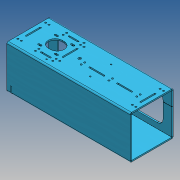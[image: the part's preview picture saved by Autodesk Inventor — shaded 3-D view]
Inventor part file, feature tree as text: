
AUTODESK INVENTOR PART (.ipt)
format: ipt  version: 2017 (Build 210142000, 142)  size: 519,168 bytes
history: native  units: mm
features: other x15, sketch x5, extrude x3, projected_geometry x1
ambient origin geometry x8: Origin, YZ Plane, XZ Plane, XY Plane, X Axis, Y Axis, Z Axis, Center Point
bodies: Body1 (feature_tree)
feature tree (24):
  other  "Sólido1"
  extrude  "Extrusión1"  Depth=67.5mm
  other  "Pestaña1"
  sketch  "Boceto4"  dims[d9=41.14mm]
  other  "Cara1"
  other  "Cara2"
  sketch  "Boceto5"  dims[d10=6.0mm d11=53.14mm d12=6.0mm d13=4.0mm d14=115.0mm d15=20.0mm d16=60.0mm d17=60.0mm d18=4.0mm d19=33.93mm d20=22.0mm d21=120.0mm d22=130.0mm d23=20.0mm d24=4.0mm d25=0.0mm d26=4.0mm d27=2.0mm d28=8.0mm d29=4.0mm d30=120.0mm d31=90.0deg d32=0.1mm d33=16.0mm d34=4.0mm d35=4.0mm d36=4.0mm d37=8.0mm d38=25.0mm d39=25.0mm d40=4.0mm d41=0.0mm d42=47.14mm d43=47.14mm d44=20.0mm d45=6.0mm d46=14.2mm d47=25.0mm d48=0.1mm d49=4.0mm d50=2.0mm d51=8.0mm d52=4.0mm d53=0.1mm d54=4.0mm d55=2.0mm d56=8.0mm d57=4.0mm d58=0.5mm d59=0.5mm d60=20.0mm d61=20.0mm d62=4.0mm d63=41.0mm d65=5.0mm d66=10.0mm d67=5.0mm d68=40.0mm d70=4.0mm d71=25.0mm d72=25.0mm d73=0.1mm d74=4.0mm d75=2.0mm d76=8.0mm d77=4.0mm d78=4.0mm d79=41.0mm d80=39.833333mm d81=79.666667mm d82=84.0mm d83=5.0mm d84=20.0mm d85=0.0mm d86=50.0mm d87=355.0mm d88=12.5mm d89=12.5mm d90=23.6mm d91=11.8mm d92=26.0mm d93=15.0mm d94=80.0mm d95=40.0mm d96=4.0mm d97=194.8mm d98=97.4mm]
  other  "Cara3"
  extrude  "Extrusión3"  Depth=42.0mm
  extrude  "Extrusión2"  Depth=5.0mm
  sketch  "Boceto1"  dims[d1=56.4mm d2=67.5mm]
  sketch  "Boceto2"  dims[d4=200.0mm d5=42.0mm]
  other  "Placa1"
  other  "Doblez1"
  other  "Esquina1"
  sketch  "Boceto3"  dims[d6=8.0mm d8=5.0mm]
  projected_geometry  "Contorno proyectado1"
  other  "Placa2"
  other  "Doblez2"
  other  "Placa3"
  other  "Doblez3"
  other  "Placa4"
  other  "Doblez4"
  other  "Definición1"
